# Revit family: IS_iLifeB_T4611_BIM_NL
name_source: partatom
category: Plumbing Fixtures
units: mm (PartAtom-declared; Revit-internal decimal feet)

## family parameters
Always vertical = No
Cut with Voids When Loaded = Yes
OmniClass Number = 23.45.05.14.14
OmniClass Title = Sinks/Lavatories
Part Type = Normal
Room Calculation Point = No
Round Connector Dimension = Use Diameter
Shared = No
Work Plane-Based = No

## types (2) — shared parameters
Afmetingen = 550 x 440 x 170 mm
AfstandsEenheid = Millimeter
Auteur = Ideal Standard
BIMobject category = Wash Basins
BIMobject category code = wash-basins
BIMobject main category = Sanitary
BIMobject main category code = sanitary
Beschrijvinggarantie = Herstellergarantie
BimObjectNaam = IS_IdealStandard_Wall-hunghandrinsebasins_i.lifeB_T4611
Brand url = http://www.idealstandard.nl
Breedte = 549.37024
Date of publishing = 22/07/2022
Diepte = 440 mm
DuurEenheid = Jahre
Edition number = 1
Eigenschappen = Semicountertop 55 cm mit Hahnloch in der Mitte und Überlauf
GTIN code = https://8014140503736
GarantieduurInstallatie = https://www.idealstandard.nl
Garantieonderdelen = https://www.idealstandard.nl
Garantieunits = Jahre
GemaaktOp = 22/07/2022
Hoogte = 170.065258026123
Hulp = https://www.idealstandard.nl
IFC Classification = Sanitary Terminal
Installatieinstructies = https://www.idealstandard.nl
Installation instructions = https://www.idealstandard.nl
Lengte = 440 mm
Manufacturer = Ideal Standard
Manufacturer name = Ideal Standard
Materiaal = Schamotte
Material main = Fireclay
Merk = Ideal Standard
NBS Reference Code = 45-35-70/360
NBS Reference Description = Counter top wash basins
Nettogewicht = 13.2
NominalDepth = 440 mm
NominalHeight = 170 mm
NominalWidth = 549 mm
Normen = Wall-hunghandrinsebasins_i.lifeB_T4611_IdealStandard
OmniClass Code = 23-39 29 13 21 19
OmniClass Description = Surface Water Retention Basins
Ophangingwastafel = halbe Arbeitsplatte
OppervlakteEenheid = Millimeter
Product Guid = abada9a8-3ba5-4fa4-b0cc-91d397dac73b
Product SKU = T4611
Product certification = https://www.idealstandard.nl
Product data url = https://bimobject.com
Product family = I.Life B
Product group = Sanitary
Product name = I.Life b semicountertop 55 cm with center taphole
Product url = https://www.idealstandard.nl
Productinformatie = https://www.idealstandard.nl
QR code = http://bimobject.com
Revisie = 1
Size = 550 x 440 x 170 mm
Technical description = https://www.idealstandard.nl
Telefoonnummer = 077 355 08 08
Toepassing = semicountertop basin
Typeconnectie = Installation
Typewastafel = Halbaufsatzwaschbecken
UNSPSC Code = 301815
URL = https://www.idealstandard.nl
Uniclass 2015 Code = Pr_40_20_96_18
Uniclass 2015 Name = Countertop washbasins
Uniclass2015Beschrijving = Countertop washbasins
Uniclass2015Referentie = Pr_40_20_96_18
Uniclass2015Version = v1.26
Urlproducent = https://www.idealstandard.nl
ValutaEenheid = Euro
Versie = 1
Verwachtelevensduur = 5
Volumeunits = Liter
Vorm = geformt
Wisselstukken = https://www.idealstandard.nl
Youtube clip = https://www.youtube.com
zero-valued in all types: BrutoGewicht, Cost, Vervangingskosten

## per-type parameters (varying)
| type | Afwerking | Artikelnummer | Artikelomschrijving | Artikelreferentie | Barcode | Description | Kleur | Model |
| T461101 - Ideal Standard i.life B  semicountertop 55 cm  with center taphole and overflow - White Finish | Weiß | T461101 | Ideal Standard i.life B Halbtischplatte 55 cm mit Hahnlochmitte, mit Überlauf, inkl. Befestigungsset E209167, weiß, im Karton, EU-Palette | Ideal Standard i.life B  semicountertop 55 cm  with center taphole and overflow - White Finish | 8014140503736 | Ideal Standard i.life B  semicountertop 55 cm  with center taphole, with overflow, fixing set E209167 included, white, in carton box, EU pallet | Weiß | T461101 |
| T4611MA - Ideal Standard i.life B  semicountertop 55 cm  with center taphole and overflow  - Ideal Plus White | Weiß Ideal Plus | T4611MA | Ideal Standard i.life B Halbtischplatte 55 cm mit Hahnlochmitte, mit Überlauf, inkl. Befestigungsset E209167, weiß Ideal Plus, im Karton, EU-Palette | Ideal Standard i.life B  semicountertop 55 cm  with center taphole and overflow  - Ideal Plus White | 8014140509608 | Ideal Standard i.life B  semicountertop 55 cm  with center taphole, with overflow, fixing set E209167 included, white Ideal Plus, in carton box, EU pallet | Weiß Ideal Plus | T4611MA |

## geometry (parser evidence)
native form markers: Sweep x4
no freeform markers — native parametric forms only
